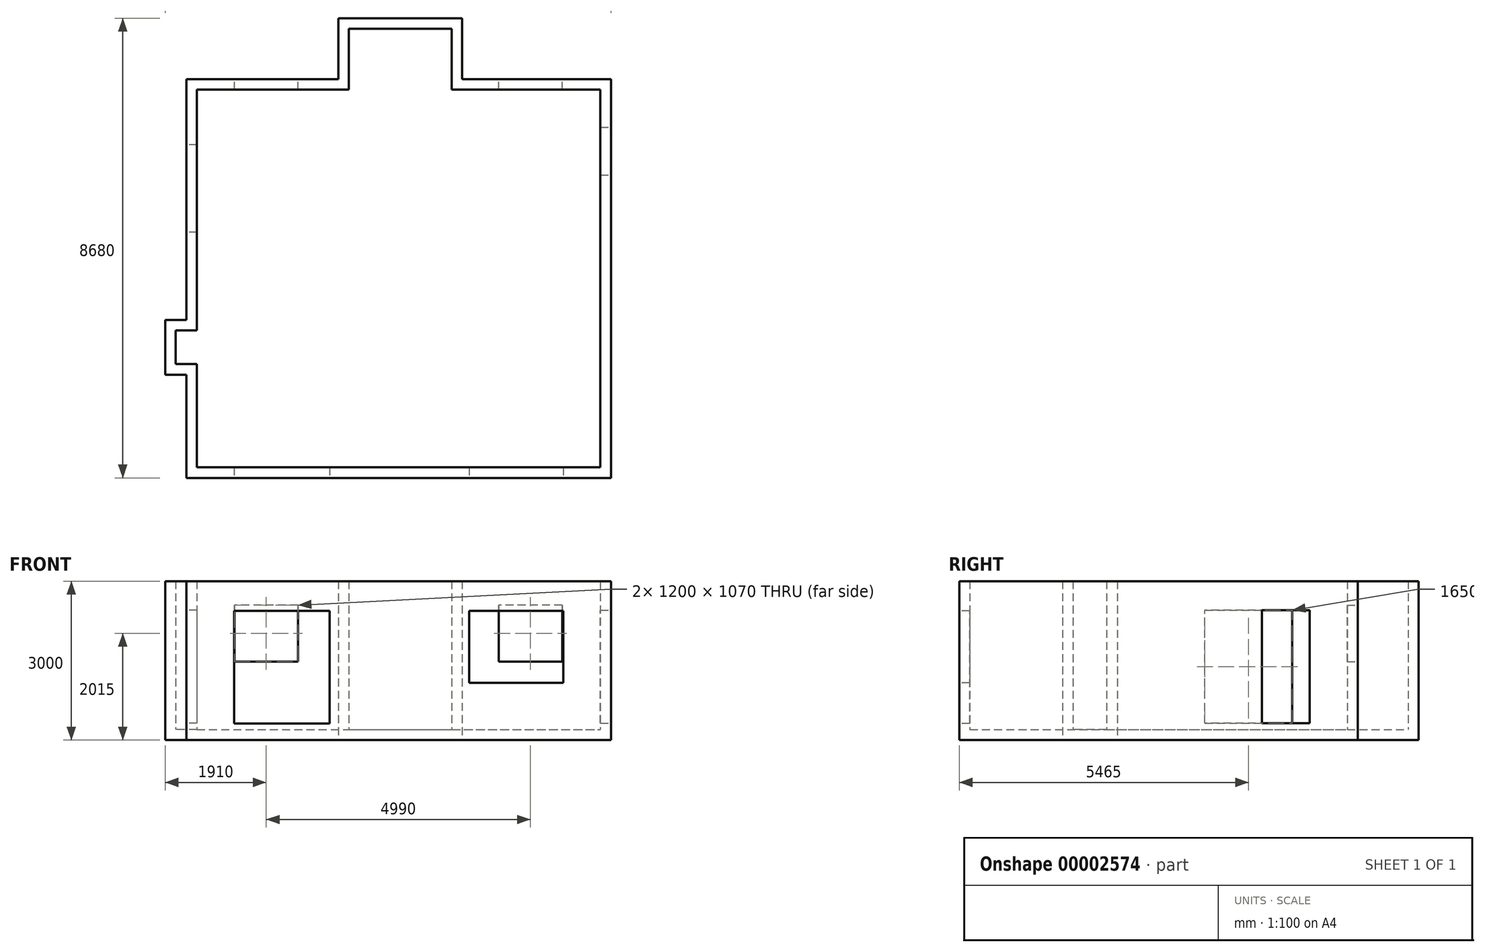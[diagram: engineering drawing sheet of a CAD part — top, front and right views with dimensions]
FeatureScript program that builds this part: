
annotation { "Feature Type Name" : "Feature", "Feature Type Description" : "" }
export const myFeature = defineFeature(function(context is Context, id is Id, definition is map)
    precondition{}
    {
        {
            var Q0;
            Q0=qCreatedBy(makeId("Top.planeOp"),FACE);
            var sketch = newSketch(context, id + "F0", { "sketchPlane" : qUnion([Q0])});
            skLineSegment(sketch, "E0.bottom", {"start": v(0, 0) * mm, "end": v(8020, 0) * mm});
            skLineSegment(sketch, "E0.top", {"start": v(0, 7530) * mm, "end": v(8020, 7530) * mm});
            skLineSegment(sketch, "E0.left", {"start": v(0, 0) * mm, "end": v(0, 7530) * mm});
            skLineSegment(sketch, "E0.right", {"start": v(8020, 0) * mm, "end": v(8020, 7530) * mm});
            skSolve(sketch);
        }
        {
            var Q0;
            Q0 = qSketchRegion(id + "F0", true);
            extrude(context, id + "F1", {"entities" : qUnion([Q0]), "depth" : 3000 * mm});
        }
        {
            var Q0;
            Q0=qCreatedBy(makeId("Top.planeOp"),FACE);
            var sketch = newSketch(context, id + "F2", { "sketchPlane" : qUnion([Q0])});
            skLineSegment(sketch, "E1.0.0", {"start": v(5210, 7530) * mm, "end": v(0, 7530) * mm});
            skLineSegment(sketch, "E1.0.2", {"start": v(2870, 7530) * mm, "end": v(5210, 7530) * mm});
            skLineSegment(sketch, "E2.top", {"start": v(2870, 8680) * mm, "end": v(5210, 8680) * mm});
            skLineSegment(sketch, "E2.left", {"start": v(2870, 7530) * mm, "end": v(2870, 8680) * mm});
            skLineSegment(sketch, "E2.right", {"start": v(5210, 7530) * mm, "end": v(5210, 8680) * mm});
            skPoint(sketch, "E3.orphan", {"position": v(0, 7530) * mm});
            skPoint(sketch, "E4.orphan", {"position": v(8020, 7530) * mm});
            skSolve(sketch);
        }
        {
            var Q0;
            Q0 = qSketchRegion(id + "F2", true);
            var Q1;
            Q1=makeQuery(id+"F1.opExtrude","CAP_FACE",FACE,{"disambiguationData":[OSD([sQuery(id+"F0.wireOp",EDGE,"E0.bottom"),sQuery(id+"F0.wireOp",EDGE,"E0.top"),sQuery(id+"F0.wireOp",EDGE,"E0.left"),sQuery(id+"F0.wireOp",EDGE,"E0.right")])],"isStart":false});
            extrude(context, id + "F3", {"entities" : qUnion([Q0]), "operationType" : NewBodyOperationType.ADD, "endBound" : BoundingType.UP_TO_SURFACE, "endBoundEntityFace" : qUnion([Q1]), "depth" : 25 * mm});
        }
        {
            var Q0;
            Q0=qCreatedBy(makeId("Top.planeOp"),FACE);
            var sketch = newSketch(context, id + "F4", { "sketchPlane" : qUnion([Q0])});
            skLineSegment(sketch, "E5.bottom", {"start": v(0, 2985) * mm, "end": v(-400, 2985) * mm});
            skLineSegment(sketch, "E5.top", {"start": v(0, 1950) * mm, "end": v(-400, 1950) * mm});
            skLineSegment(sketch, "E5.left", {"start": v(0, 2985) * mm, "end": v(0, 1950) * mm});
            skLineSegment(sketch, "E5.right", {"start": v(-400, 2985) * mm, "end": v(-400, 1950) * mm});
            skSolve(sketch);
        }
        {
            var Q0;
            Q0 = qSketchRegion(id + "F4", true);
            var Q1;
            Q1=makeQuery(id+"F3.boolean.opBoolean","MERGE",FACE,{"derivedFrom":[makeQuery(id+"F1.opExtrude","CAP_FACE",FACE,{"disambiguationData":[OSD([sQuery(id+"F0.wireOp",EDGE,"E0.bottom"),sQuery(id+"F0.wireOp",EDGE,"E0.top"),sQuery(id+"F0.wireOp",EDGE,"E0.left"),sQuery(id+"F0.wireOp",EDGE,"E0.right")])],"isStart":false}),makeQuery(id+"F3.opExtrude","CAP_FACE",FACE,{"disambiguationData":[OSD([sQuery(id+"F2.wireOp",EDGE,"E1.0.2"),sQuery(id+"F2.wireOp",EDGE,"E2.top"),sQuery(id+"F2.wireOp",EDGE,"E2.left"),sQuery(id+"F2.wireOp",EDGE,"E2.right")])],"isStart":false})]});
            extrude(context, id + "F5", {"entities" : qUnion([Q0]), "operationType" : NewBodyOperationType.ADD, "endBound" : BoundingType.UP_TO_SURFACE, "endBoundEntityFace" : qUnion([Q1]), "depth" : 25 * mm});
        }
        {
            var Q0;
            Q0=makeQuery(id+"F3.boolean.opBoolean","MERGE",FACE,{"derivedFrom":[makeQuery(id+"F1.opExtrude","CAP_FACE",FACE,{"disambiguationData":[OSD([sQuery(id+"F0.wireOp",EDGE,"E0.bottom"),sQuery(id+"F0.wireOp",EDGE,"E0.top"),sQuery(id+"F0.wireOp",EDGE,"E0.left"),sQuery(id+"F0.wireOp",EDGE,"E0.right")])],"isStart":false}),makeQuery(id+"F3.opExtrude","CAP_FACE",FACE,{"disambiguationData":[OSD([sQuery(id+"F2.wireOp",EDGE,"E1.0.2"),sQuery(id+"F2.wireOp",EDGE,"E2.top"),sQuery(id+"F2.wireOp",EDGE,"E2.left"),sQuery(id+"F2.wireOp",EDGE,"E2.right")])],"isStart":false})]});
            shell(context, id + "F6", {"entities" : qUnion([Q0]), "thickness" : 200 * mm});
        }
        {
            var Q0;
            Q0=makeQuery(id+"F1.opExtrude","SWEPT_FACE",FACE,{"disambiguationData":[OSD([sQuery(id+"F0.wireOp",EDGE,"E0.bottom")])]});
            var sketch = newSketch(context, id + "F7", { "sketchPlane" : qUnion([Q0])});
            skLineSegment(sketch, "E6.bottom", {"start": v(905, 310) * mm, "end": v(2705, 310) * mm});
            skLineSegment(sketch, "E6.top", {"start": v(905, 2440) * mm, "end": v(2705, 2440) * mm});
            skLineSegment(sketch, "E6.left", {"start": v(905, 310) * mm, "end": v(905, 2440) * mm});
            skLineSegment(sketch, "E6.right", {"start": v(2705, 310) * mm, "end": v(2705, 2440) * mm});
            skSolve(sketch);
        }
        {
            var Q0;
            Q0 = qSketchRegion(id + "F7", true);
            extrude(context, id + "F8", {"entities" : qUnion([Q0]), "operationType" : NewBodyOperationType.REMOVE, "endBound" : BoundingType.UP_TO_NEXT, "oppositeDirection" : true, "depth" : 25 * mm});
        }
        {
            var Q0;
            {var subQ0=sQuery(id+"F0.wireOp",EDGE,"E0.top");var subQ2=sQuery(id+"F0.wireOp",EDGE,"E0.left");Q0=makeQuery(id+"F5.boolean.opBoolean","SPLIT",FACE,{"disambiguationData":[TD([makeQuery(id+"F1.opExtrude","SWEPT_FACE",FACE,{"disambiguationData":[OSD([subQ0])]})])],"derivedFrom":makeQuery(id+"F1.opExtrude","SWEPT_FACE",FACE,{"disambiguationData":[OSD([subQ2])]})});}
            var sketch = newSketch(context, id + "F9", { "sketchPlane" : qUnion([Q0])});
            skLineSegment(sketch, "E7.bottom", {"start": v(-6290, 320) * mm, "end": v(-4640, 320) * mm});
            skLineSegment(sketch, "E7.top", {"start": v(-6290, 2450) * mm, "end": v(-4640, 2450) * mm});
            skLineSegment(sketch, "E7.left", {"start": v(-6290, 320) * mm, "end": v(-6290, 2450) * mm});
            skLineSegment(sketch, "E7.right", {"start": v(-4640, 320) * mm, "end": v(-4640, 2450) * mm});
            skSolve(sketch);
        }
        {
            var Q0;
            Q0 = qSketchRegion(id + "F9", true);
            extrude(context, id + "F10", {"entities" : qUnion([Q0]), "operationType" : NewBodyOperationType.REMOVE, "endBound" : BoundingType.UP_TO_NEXT, "oppositeDirection" : true, "depth" : 25 * mm});
        }
        {
            var Q0;
            Q0=makeQuery(id+"F1.opExtrude","SWEPT_FACE",FACE,{"disambiguationData":[OSD([sQuery(id+"F0.wireOp",EDGE,"E0.right")])]});
            var sketch = newSketch(context, id + "F11", { "sketchPlane" : qUnion([Q0])});
            skLineSegment(sketch, "E8.bottom", {"start": v(5720, 320) * mm, "end": v(6620, 320) * mm});
            skLineSegment(sketch, "E8.top", {"start": v(5720, 2450) * mm, "end": v(6620, 2450) * mm});
            skLineSegment(sketch, "E8.left", {"start": v(5720, 320) * mm, "end": v(5720, 2450) * mm});
            skLineSegment(sketch, "E8.right", {"start": v(6620, 320) * mm, "end": v(6620, 2450) * mm});
            skSolve(sketch);
        }
        {
            var Q0;
            Q0 = qSketchRegion(id + "F11", true);
            extrude(context, id + "F12", {"entities" : qUnion([Q0]), "operationType" : NewBodyOperationType.REMOVE, "endBound" : BoundingType.UP_TO_NEXT, "oppositeDirection" : true, "depth" : 25 * mm});
        }
        {
            var Q0;
            Q0=makeQuery(id+"F1.opExtrude","SWEPT_FACE",FACE,{"disambiguationData":[OSD([sQuery(id+"F0.wireOp",EDGE,"E0.bottom")])]});
            var sketch = newSketch(context, id + "F13", { "sketchPlane" : qUnion([Q0])});
            skLineSegment(sketch, "E9.bottom", {"start": v(5340, 2440) * mm, "end": v(7120, 2440) * mm});
            skLineSegment(sketch, "E9.top", {"start": v(5340, 1080) * mm, "end": v(7120, 1080) * mm});
            skLineSegment(sketch, "E9.left", {"start": v(5340, 2440) * mm, "end": v(5340, 1080) * mm});
            skLineSegment(sketch, "E9.right", {"start": v(7120, 2440) * mm, "end": v(7120, 1080) * mm});
            skSolve(sketch);
        }
        {
            var Q0;
            Q0 = qSketchRegion(id + "F13", true);
            extrude(context, id + "F14", {"entities" : qUnion([Q0]), "operationType" : NewBodyOperationType.REMOVE, "endBound" : BoundingType.UP_TO_NEXT, "oppositeDirection" : true, "depth" : 25 * mm});
        }
        {
            var Q0;
            {var subQ0=sQuery(id+"F0.wireOp",EDGE,"E0.right");var subQ2=sQuery(id+"F0.wireOp",EDGE,"E0.top");Q0=makeQuery(id+"F3.boolean.opBoolean","SPLIT",FACE,{"disambiguationData":[TD([makeQuery(id+"F1.opExtrude","SWEPT_FACE",FACE,{"disambiguationData":[OSD([subQ0])]})])],"derivedFrom":makeQuery(id+"F1.opExtrude","SWEPT_FACE",FACE,{"disambiguationData":[OSD([subQ2])]})});}
            var sketch = newSketch(context, id + "F15", { "sketchPlane" : qUnion([Q0])});
            skLineSegment(sketch, "E10.bottom", {"start": v(-7100, 2550) * mm, "end": v(-5900, 2550) * mm});
            skLineSegment(sketch, "E10.top", {"start": v(-7100, 1480) * mm, "end": v(-5900, 1480) * mm});
            skLineSegment(sketch, "E10.left", {"start": v(-7100, 2550) * mm, "end": v(-7100, 1480) * mm});
            skLineSegment(sketch, "E10.right", {"start": v(-5900, 2550) * mm, "end": v(-5900, 1480) * mm});
            skSolve(sketch);
        }
        {
            var Q0;
            Q0 = qSketchRegion(id + "F15", true);
            extrude(context, id + "F16", {"entities" : qUnion([Q0]), "operationType" : NewBodyOperationType.REMOVE, "endBound" : BoundingType.UP_TO_NEXT, "oppositeDirection" : true, "depth" : 25 * mm});
        }
        {
            var Q0;
            {var subQ0=sQuery(id+"F0.wireOp",EDGE,"E0.left");var subQ6=sQuery(id+"F0.wireOp",EDGE,"E0.top");Q0=makeQuery(id+"F3.boolean.opBoolean","SPLIT",FACE,{"disambiguationData":[TD([makeQuery(id+"F1.opExtrude","SWEPT_FACE",FACE,{"disambiguationData":[OSD([subQ0])]})])],"derivedFrom":makeQuery(id+"F1.opExtrude","SWEPT_FACE",FACE,{"disambiguationData":[OSD([subQ6])]})});}
            var sketch = newSketch(context, id + "F17", { "sketchPlane" : qUnion([Q0])});
            skLineSegment(sketch, "E11.bottom", {"start": v(-2110, 2550) * mm, "end": v(-910, 2550) * mm});
            skLineSegment(sketch, "E11.top", {"start": v(-2110, 1480) * mm, "end": v(-910, 1480) * mm});
            skLineSegment(sketch, "E11.left", {"start": v(-2110, 2550) * mm, "end": v(-2110, 1480) * mm});
            skLineSegment(sketch, "E11.right", {"start": v(-910, 2550) * mm, "end": v(-910, 1480) * mm});
            skSolve(sketch);
        }
        {
            var Q0;
            Q0 = qSketchRegion(id + "F17", true);
            extrude(context, id + "F18", {"entities" : qUnion([Q0]), "operationType" : NewBodyOperationType.REMOVE, "endBound" : BoundingType.UP_TO_NEXT, "oppositeDirection" : true, "depth" : 25 * mm});
        }
    });
